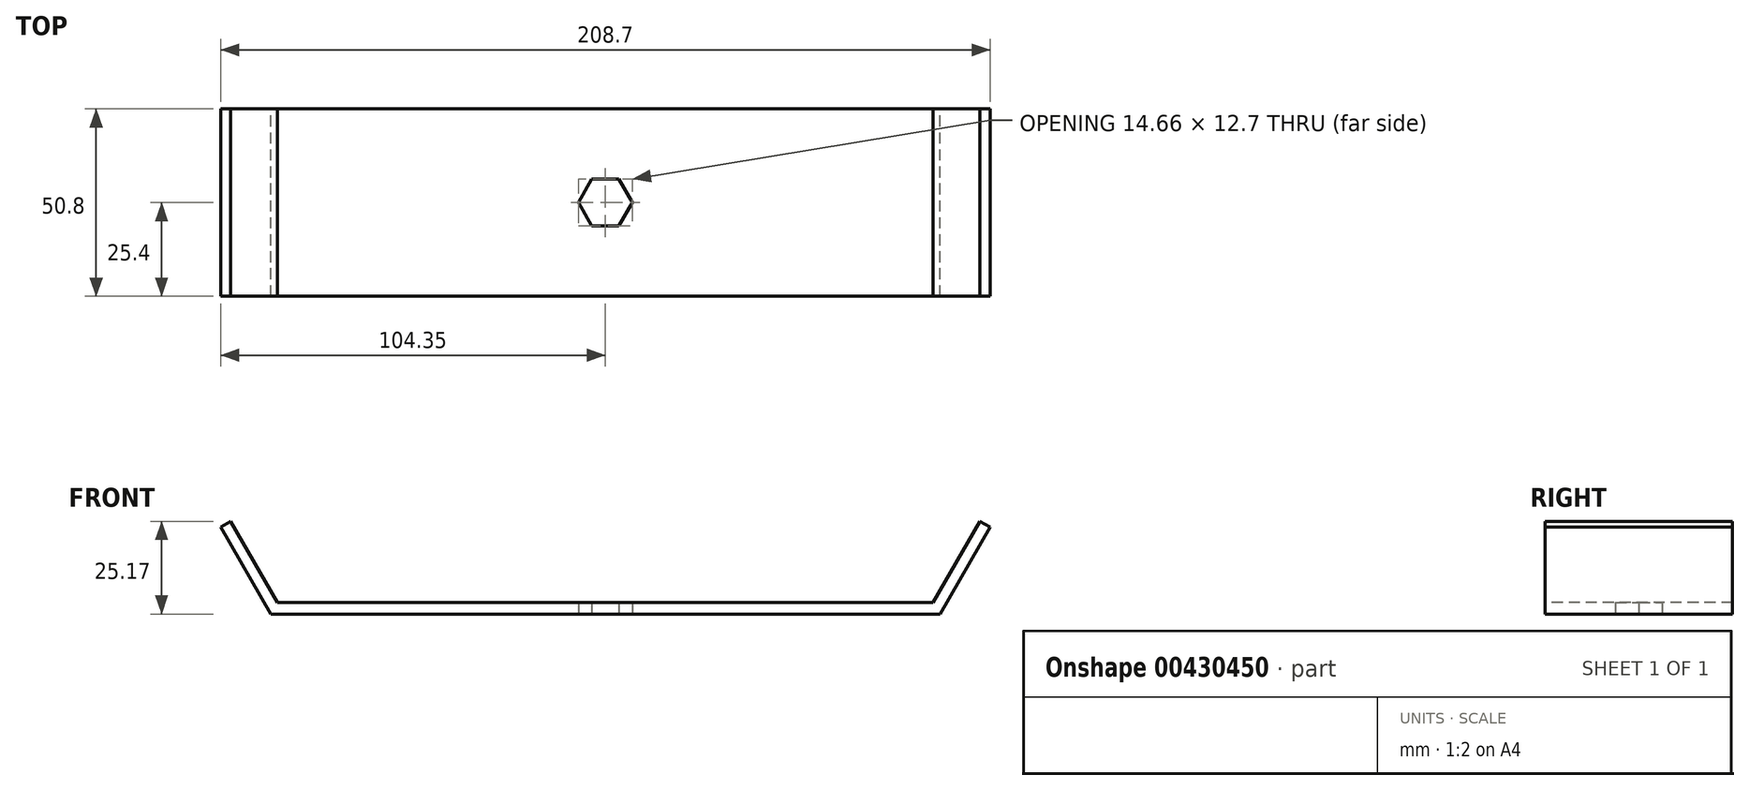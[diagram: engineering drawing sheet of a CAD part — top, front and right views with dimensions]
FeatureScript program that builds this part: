
annotation { "Feature Type Name" : "Feature", "Feature Type Description" : "" }
export const myFeature = defineFeature(function(context is Context, id is Id, definition is map)
    precondition{}
    {
        {
            var Q0;
            Q0=qCreatedBy(makeId("Top.planeOp"),FACE);
            var sketch = newSketch(context, id + "F0", { "sketchPlane" : qUnion([Q0])});
            skLineSegment(sketch, "E0.bottom", {"start": v(-88.9, 25.4) * mm, "end": v(88.9, 25.4) * mm});
            skLineSegment(sketch, "E0.top", {"start": v(-88.9, -25.4) * mm, "end": v(88.9, -25.4) * mm});
            skLineSegment(sketch, "E0.left", {"start": v(-88.9, 25.4) * mm, "end": v(-88.9, -25.4) * mm});
            skLineSegment(sketch, "E0.right", {"start": v(88.9, 25.4) * mm, "end": v(88.9, -25.4) * mm});
            skPoint(sketch, "E0.middle", {"position": v(0, 0) * mm});
            skCircle(sketch, "E1.cCircle", {"center": v(0, 0) * mm, "radius": 6.35 * mm, "construction": true});
            skLineSegment(sketch, "E1.0", {"start": v(-7.33, 0) * mm, "end": v(-3.67, 6.35) * mm});
            skLineSegment(sketch, "E1.1", {"start": v(-3.67, 6.35) * mm, "end": v(3.67, 6.35) * mm});
            skLineSegment(sketch, "E1.2", {"start": v(3.67, 6.35) * mm, "end": v(7.33, 0) * mm});
            skLineSegment(sketch, "E1.3", {"start": v(7.33, 0) * mm, "end": v(3.67, -6.35) * mm});
            skLineSegment(sketch, "E1.4", {"start": v(3.67, -6.35) * mm, "end": v(-3.67, -6.35) * mm});
            skLineSegment(sketch, "E1.5", {"start": v(-3.67, -6.35) * mm, "end": v(-7.33, 0) * mm});
            skPoint(sketch, "E1.0.midPoint", {"position": v(-5.5, 3.18) * mm});
            skSolve(sketch);
        }
        {
            var Q0;
            Q0 = qSketchRegion(id + "F0", true);
            extrude(context, id + "F1", {"entities" : qUnion([Q0]), "depth" : 3.17 * mm});
        }
        {
            var Q0;
            Q0=qCreatedBy(makeId("Front.planeOp"),FACE);
            var sketch = newSketch(context, id + "F2", { "sketchPlane" : qUnion([Q0])});
            skLineSegment(sketch, "E2", {"start": v(-90.73, 0) * mm, "end": v(-104.35, 23.58) * mm});
            skLineSegment(sketch, "E3", {"start": v(-88.9, 3.18) * mm, "end": v(-101.6, 25.17) * mm});
            skLineSegment(sketch, "E4", {"start": v(-101.6, 25.17) * mm, "end": v(-104.35, 23.58) * mm});
            skLineSegment(sketch, "E5.MirrorCS", {"start": v(101.6, 25.17) * mm, "end": v(104.35, 23.58) * mm});
            skLineSegment(sketch, "E6.MirrorCS", {"start": v(90.73, 0) * mm, "end": v(104.35, 23.58) * mm});
            skLineSegment(sketch, "E7.MirrorCS", {"start": v(88.9, 3.17) * mm, "end": v(101.6, 25.17) * mm});
            skLineSegment(sketch, "E8", {"start": v(-90.73, 0) * mm, "end": v(-88.9, 0) * mm});
            skLineSegment(sketch, "E9", {"start": v(-88.9, 0) * mm, "end": v(-88.9, 3.18) * mm});
            skLineSegment(sketch, "E10.MirrorCS", {"start": v(88.9, 0) * mm, "end": v(88.9, 3.18) * mm});
            skLineSegment(sketch, "E11.MirrorCS", {"start": v(90.73, 0) * mm, "end": v(88.9, 0) * mm});
            skSolve(sketch);
        }
        {
            var Q0;
            Q0 = qSketchRegion(id + "F2", true);
            extrude(context, id + "F3", {"entities" : qUnion([Q0]), "operationType" : NewBodyOperationType.ADD, "depth" : 50.8 * mm, "symmetric" : true});
        }
    });
